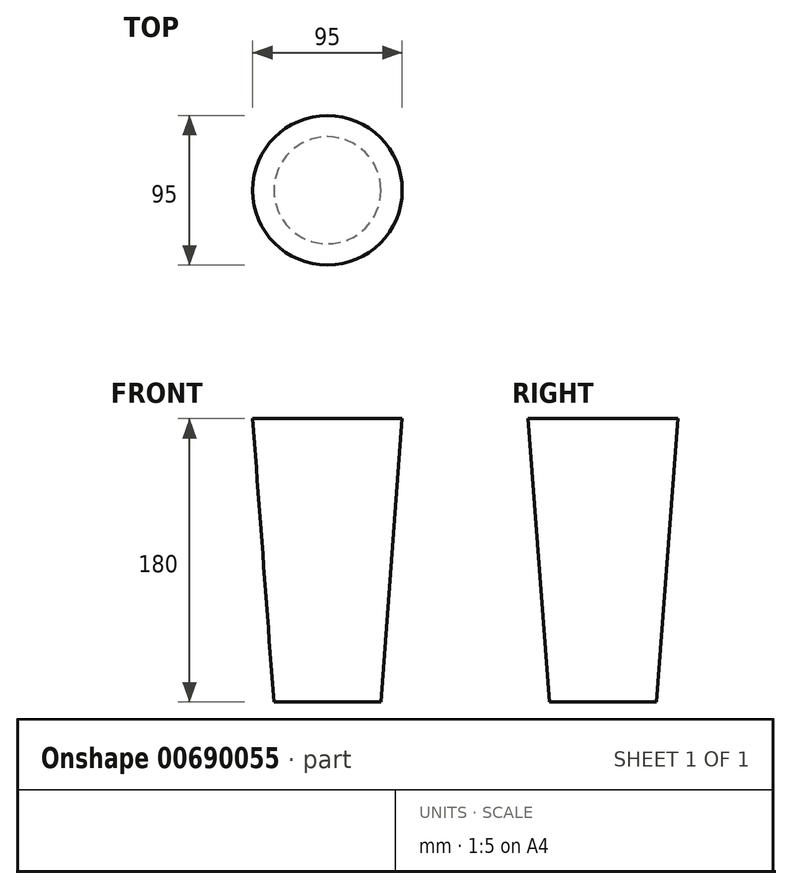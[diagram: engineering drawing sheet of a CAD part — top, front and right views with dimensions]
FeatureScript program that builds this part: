
annotation { "Feature Type Name" : "Feature", "Feature Type Description" : "" }
export const myFeature = defineFeature(function(context is Context, id is Id, definition is map)
    precondition{}
    {
        {
            var Q0;
            Q0=qCreatedBy(makeId("Right.planeOp"),FACE);
            var sketch = newSketch(context, id + "F0", { "sketchPlane" : qUnion([Q0])});
            skLineSegment(sketch, "E0", {"start": v(-47.5, 180) * mm, "end": v(-34, 0) * mm});
            skLineSegment(sketch, "E1", {"start": v(-34, 0) * mm, "end": v(0, 0) * mm});
            skLineSegment(sketch, "E2", {"start": v(0, 0) * mm, "end": v(0, 180) * mm});
            skLineSegment(sketch, "E3", {"start": v(-47.5, 180) * mm, "end": v(0, 180) * mm});
            skSolve(sketch);
        }
        {
            var Q0;
            Q0=makeQuery(id+"F0.imprint","IMPRINT",FACE,{"disambiguationData":[TD([[makeQuery(id+"F0.imprint","IMPRINT",EDGE,{"derivedFrom":sQuery(id+"F0.wireOp",EDGE,"E0")}),1.0]])]});
            var Q1;
            Q1=sQuery(id+"F0.wireOp",EDGE,"E2");
            revolve(context, id + "F1", {"entities" : qUnion([Q0]), "axis" : qUnion([Q1]), "revolveType" : RevolveType.FULL});
        }
    });
